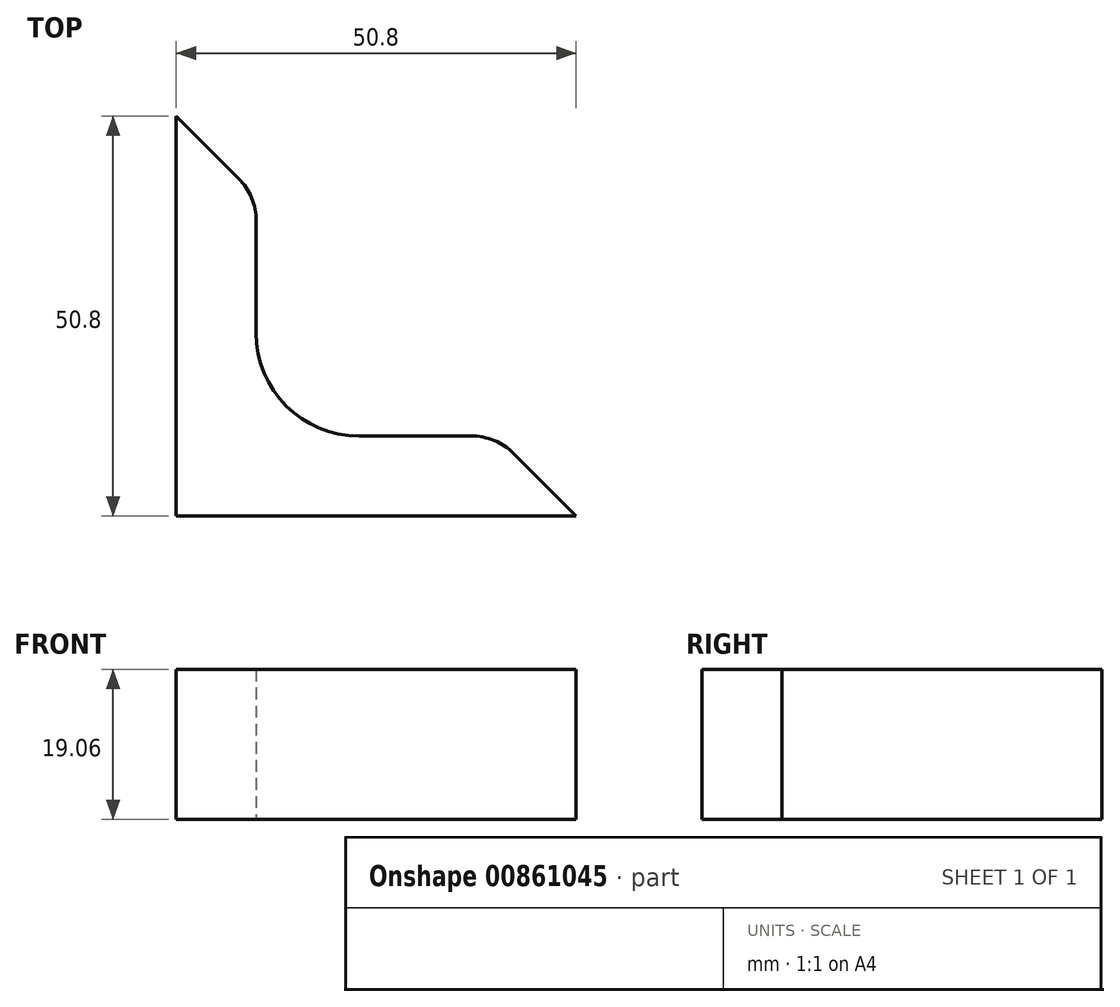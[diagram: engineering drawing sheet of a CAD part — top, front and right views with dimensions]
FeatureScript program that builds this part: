
annotation { "Feature Type Name" : "Feature", "Feature Type Description" : "" }
export const myFeature = defineFeature(function(context is Context, id is Id, definition is map)
    precondition{}
    {
        {
            var Q0;
            Q0=qCreatedBy(makeId("Top.planeOp"),FACE);
            var sketch = newSketch(context, id + "F0", { "sketchPlane" : qUnion([Q0])});
            skLineSegment(sketch, "E0.bottom", {"start": v(25.4, -25.4) * mm, "end": v(-25.4, -25.4) * mm});
            skLineSegment(sketch, "E0.right", {"start": v(-25.4, -25.4) * mm, "end": v(-25.4, 25.4) * mm});
            skPoint(sketch, "E1.newPointA", {"position": v(-15.24, 15.24) * mm});
            skPoint(sketch, "E2.visualSharp", {"position": v(15.24, -15.24) * mm});
            skLineSegment(sketch, "E3", {"start": v(15.24, -15.24) * mm, "end": v(25.4, -25.4) * mm});
            skLineSegment(sketch, "E4", {"start": v(-15.24, 15.24) * mm, "end": v(-25.4, 25.4) * mm});
            skLineSegment(sketch, "E5", {"start": v(-15.24, 15.24) * mm, "end": v(-15.24, -15.24) * mm});
            skLineSegment(sketch, "E6", {"start": v(15.24, -15.24) * mm, "end": v(-15.24, -15.24) * mm});
            skSolve(sketch);
        }
        {
            var Q0;
            Q0=makeQuery(id+"F0.imprint","IMPRINT",FACE,{"disambiguationData":[TD([[makeQuery(id+"F0.imprint","IMPRINT",EDGE,{"derivedFrom":sQuery(id+"F0.wireOp",EDGE,"E0.bottom")}),-1.0]])]});
            extrude(context, id + "F1", {"entities" : qUnion([Q0]), "endBound" : BoundingType.SYMMETRIC, "depth" : 19.05 * mm, "offsetDistance" : 25.4 * mm});
        }
        {
            var Q0;
            Q0=makeQuery(id+"F1.opExtrude","SWEPT_EDGE",EDGE,{"disambiguationData":[OSD([sQuery(id+"F0.wireOp",EDGE,"E5"),sQuery(id+"F0.wireOp",EDGE,"E6")])]});
            fillet(context, id + "F2", {"entities" : qUnion([Q0]), "radius" : 13.06 * mm, "tangentPropagation" : true, "allowEdgeOverflow" : false});
        }
        {
            var Q0;
            Q0=makeQuery(id+"F1.opExtrude","SWEPT_EDGE",EDGE,{"disambiguationData":[OSD([sQuery(id+"F0.wireOp",EDGE,"E4"),sQuery(id+"F0.wireOp",EDGE,"E5")])]});
            var Q1;
            Q1=makeQuery(id+"F1.opExtrude","SWEPT_EDGE",EDGE,{"disambiguationData":[OSD([sQuery(id+"F0.wireOp",EDGE,"E3"),sQuery(id+"F0.wireOp",EDGE,"E6")])]});
            fillet(context, id + "F3", {"entities" : qUnion([Q0, Q1]), "radius" : 7.62 * mm, "tangentPropagation" : true, "allowEdgeOverflow" : false});
        }
    });
